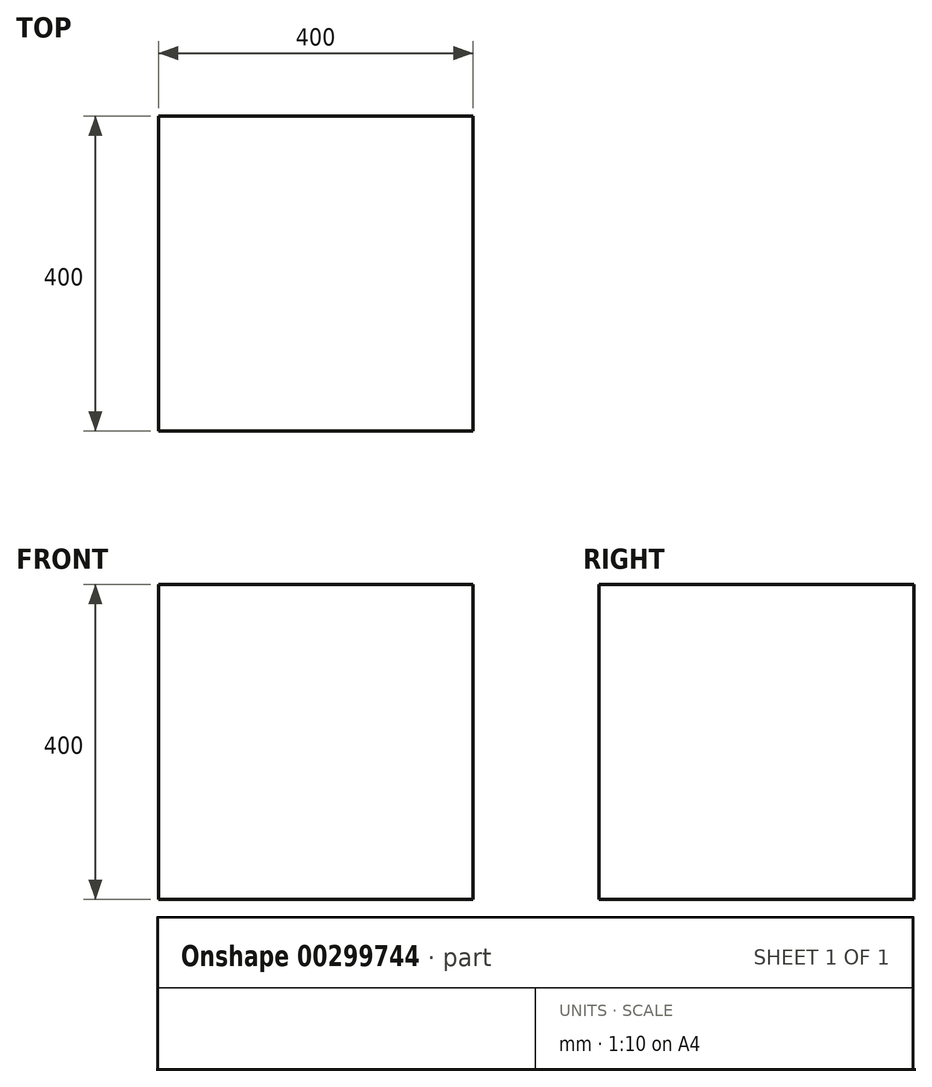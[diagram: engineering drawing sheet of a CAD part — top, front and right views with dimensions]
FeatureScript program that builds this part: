
annotation { "Feature Type Name" : "Feature", "Feature Type Description" : "" }
export const myFeature = defineFeature(function(context is Context, id is Id, definition is map)
    precondition{}
    {
        {
            assignVariable(context, id + "F0", {"name" : "hauteur", "anyValue" : 380});
        }
        {
            var Q0;
            Q0=qCreatedBy(makeId("Top.planeOp"),FACE);
            var sketch = newSketch(context, id + "F1", { "sketchPlane" : qUnion([Q0])});
            skLineSegment(sketch, "E0.bottom", {"start": v(-200, 200) * mm, "end": v(200, 200) * mm});
            skLineSegment(sketch, "E0.top", {"start": v(-200, -200) * mm, "end": v(200, -200) * mm});
            skLineSegment(sketch, "E0.left", {"start": v(-200, 200) * mm, "end": v(-200, -200) * mm});
            skLineSegment(sketch, "E0.right", {"start": v(200, 200) * mm, "end": v(200, -200) * mm});
            skPoint(sketch, "E0.middle", {"position": v(0, 0) * mm});
            skSolve(sketch);
        }
        {
            var Q0;
            Q0=makeQuery(id+"F1.imprint","IMPRINT",FACE,{"disambiguationData":[TD([[makeQuery(id+"F1.imprint","IMPRINT",EDGE,{"derivedFrom":sQuery(id+"F1.wireOp",EDGE,"E0.bottom")}),-1.0]])]});
            extrude(context, id + "F2", {"entities" : qUnion([Q0]), "depth" : (getVariable(context, 'hauteur') + 20) * mm, "symmetric" : true});
        }
        {
            var Q0;
            Q0=makeQuery(id+"F2.opExtrude","CAP_FACE",FACE,{"disambiguationData":[OSD([sQuery(id+"F1.wireOp",EDGE,"E0.bottom"),sQuery(id+"F1.wireOp",EDGE,"E0.top"),sQuery(id+"F1.wireOp",EDGE,"E0.left"),sQuery(id+"F1.wireOp",EDGE,"E0.right")])],"isStart":true});
            var sketch = newSketch(context, id + "F3", { "sketchPlane" : qUnion([Q0])});
            skLineSegment(sketch, "E1", {"start": v(-200, -190) * mm, "end": v(-200, 190) * mm, "construction": true});
            skLineSegment(sketch, "E2", {"start": v(-190, 200) * mm, "end": v(190, 200) * mm, "construction": true});
            skLineSegment(sketch, "E3", {"start": v(200, 190) * mm, "end": v(200, -190) * mm, "construction": true});
            skLineSegment(sketch, "E4", {"start": v(190, -200) * mm, "end": v(-190, -200) * mm, "construction": true});
            skCircle(sketch, "E5", {"center": v(-200, 200) * mm, "radius": 10 * mm, "construction": true});
            skCircle(sketch, "E6", {"center": v(-200, -200) * mm, "radius": 10 * mm, "construction": true});
            skSolve(sketch);
        }
        {
            var Q0;
            Q0=makeQuery(id+"F2.opExtrude","CAP_FACE",FACE,{"disambiguationData":[OSD([sQuery(id+"F1.wireOp",EDGE,"E0.bottom"),sQuery(id+"F1.wireOp",EDGE,"E0.top"),sQuery(id+"F1.wireOp",EDGE,"E0.left"),sQuery(id+"F1.wireOp",EDGE,"E0.right")])],"isStart":false});
            var sketch = newSketch(context, id + "F4", { "sketchPlane" : qUnion([Q0])});
            skLineSegment(sketch, "E7", {"start": v(-200, -190) * mm, "end": v(-200, 190) * mm, "construction": true});
            skLineSegment(sketch, "E8", {"start": v(-190, 200) * mm, "end": v(190, 200) * mm, "construction": true});
            skLineSegment(sketch, "E9", {"start": v(200, 190) * mm, "end": v(200, -190) * mm, "construction": true});
            skLineSegment(sketch, "E10", {"start": v(190, -200) * mm, "end": v(-190, -200) * mm, "construction": true});
            skSolve(sketch);
        }
        {
            var Q0;
            Q0=makeQuery(id+"F2.opExtrude","SWEPT_FACE",FACE,{"disambiguationData":[OSD([sQuery(id+"F1.wireOp",EDGE,"E0.left")])]});
            var sketch = newSketch(context, id + "F5", { "sketchPlane" : qUnion([Q0])});
            skCircle(sketch, "E11", {"center": v(200, -200) * mm, "radius": 10 * mm, "construction": true});
            skCircle(sketch, "E12", {"center": v(-200, 200) * mm, "radius": 10 * mm, "construction": true});
            skLineSegment(sketch, "E13", {"start": v(200, 190) * mm, "end": v(200, -190) * mm, "construction": true});
            skLineSegment(sketch, "E14", {"start": v(-200, 190) * mm, "end": v(-200, -190) * mm, "construction": true});
            skSolve(sketch);
        }
        {
            var Q0;
            Q0=qCreatedBy(makeId("Top.planeOp"),FACE);
            var sketch = newSketch(context, id + "F6", { "sketchPlane" : qUnion([Q0])});
            skLineSegment(sketch, "E15", {"start": v(0, 0) * mm, "end": v(-200, 0) * mm, "construction": true});
            skLineSegment(sketch, "E16", {"start": v(0, 200) * mm, "end": v(0, 0) * mm, "construction": true});
            skLineSegment(sketch, "E17", {"start": v(0, 0) * mm, "end": v(200, 0) * mm, "construction": true});
            skLineSegment(sketch, "E18", {"start": v(0, -200) * mm, "end": v(0, 0) * mm, "construction": true});
            skSolve(sketch);
        }
        {
            var Q0;
            Q0=qCreatedBy(makeId("Front.planeOp"),FACE);
            var sketch = newSketch(context, id + "F7", { "sketchPlane" : qUnion([Q0])});
            skLineSegment(sketch, "E19", {"start": v(0, 0) * mm, "end": v(0, 200) * mm, "construction": true});
            skLineSegment(sketch, "E20", {"start": v(0, 0) * mm, "end": v(0, -200) * mm, "construction": true});
            skSolve(sketch);
        }
        {
            var Q0;
            Q0=makeQuery(id+"F4.imprint","IMPRINT",FACE,{"disambiguationData":[TD([[makeQuery(id+"F4.imprint","IMPRINT",EDGE,{"derivedFrom":makeQuery(id+"F2.opExtrude","CAP_EDGE",EDGE,{"disambiguationData":[OSD([sQuery(id+"F1.wireOp",EDGE,"E0.bottom")])],"isStart":false})}),-1.0]])]});
            cPlane(context, id + "F8", {"entities" : qUnion([Q0]), "cplaneType" : CPlaneType.OFFSET, "offset" : 70 * mm, "oppositeDirection" : true, "width" : 150 * mm, "height" : 150 * mm});
        }
        {
            var Q0;
            Q0=qCreatedBy(id+"F8.planeOp",FACE);
            var sketch = newSketch(context, id + "F9", { "sketchPlane" : qUnion([Q0])});
            skLineSegment(sketch, "E21.bottom", {"start": v(-185, 204.5) * mm, "end": v(-151.7, 204.5) * mm});
            skLineSegment(sketch, "E21.top", {"start": v(-185, 162.2) * mm, "end": v(-151.7, 162.2) * mm});
            skLineSegment(sketch, "E21.left", {"start": v(-189.5, 200) * mm, "end": v(-189.5, 166.7) * mm});
            skLineSegment(sketch, "E21.right", {"start": v(-147.2, 200) * mm, "end": v(-147.2, 166.7) * mm});
            skCircle(sketch, "E22", {"center": v(-168.35, 183.35) * mm, "radius": 2.5 * mm});
            skCircle(sketch, "E23", {"center": v(-183.85, 198.85) * mm, "radius": 1.5 * mm});
            skCircle(sketch, "E24", {"center": v(-152.85, 198.85) * mm, "radius": 1.5 * mm});
            skCircle(sketch, "E25", {"center": v(-152.85, 167.85) * mm, "radius": 1.5 * mm});
            skCircle(sketch, "E26", {"center": v(-183.85, 167.85) * mm, "radius": 1.5 * mm});
            skArc(sketch, "E27", {"start": v(-189.5, 166.7) * mm, "mid": v(-187.38, 164.32) * mm, "end": v(-185, 162.2) * mm});
            skArc(sketch, "E28.trimOffspring", {"start": v(-185, 204.5) * mm, "mid": v(-187.38, 202.38) * mm, "end": v(-189.5, 200) * mm});
            skArc(sketch, "E29.trimOffspring", {"start": v(-147.2, 200) * mm, "mid": v(-149.32, 202.38) * mm, "end": v(-151.7, 204.5) * mm});
            skArc(sketch, "E30.trimOffspring", {"start": v(-151.7, 162.2) * mm, "mid": v(-149.32, 164.32) * mm, "end": v(-147.2, 166.7) * mm});
            skLineSegment(sketch, "E31", {"start": v(-170.35, 184.85) * mm, "end": v(-170.35, 181.85) * mm});
            skCircle(sketch, "E32", {"center": v(-168.35, 183.35) * mm, "radius": 11 * mm});
            skCircle(sketch, "E33", {"center": v(-168.35, 183.35) * mm, "radius": 16.15 * mm});
            skLineSegment(sketch, "E34", {"start": v(-168.35, 194.35) * mm, "end": v(-168.35, 172.35) * mm, "construction": true});
            skLineSegment(sketch, "E35", {"start": v(-179.35, 183.35) * mm, "end": v(-157.35, 183.35) * mm, "construction": true});
            skLineSegment(sketch, "E36.bottom", {"start": v(-183.85, 198.85) * mm, "end": v(-152.85, 198.85) * mm, "construction": true});
            skLineSegment(sketch, "E36.top", {"start": v(-183.85, 167.85) * mm, "end": v(-152.85, 167.85) * mm, "construction": true});
            skLineSegment(sketch, "E36.left", {"start": v(-183.85, 198.85) * mm, "end": v(-183.85, 167.85) * mm, "construction": true});
            skLineSegment(sketch, "E36.right", {"start": v(-152.85, 198.85) * mm, "end": v(-152.85, 167.85) * mm, "construction": true});
            skLineSegment(sketch, "E37.0.1.0", {"start": v(-147.2, 16.65) * mm, "end": v(-147.2, -16.65) * mm});
            skLineSegment(sketch, "E37.0.1.1", {"start": v(-185, -21.15) * mm, "end": v(-151.7, -21.15) * mm});
            skCircle(sketch, "E37.0.1.2", {"center": v(-168.35, 0) * mm, "radius": 11 * mm});
            skLineSegment(sketch, "E37.0.1.3", {"start": v(-185, 21.15) * mm, "end": v(-151.7, 21.15) * mm});
            skArc(sketch, "E37.0.1.4", {"start": v(-185, 21.15) * mm, "mid": v(-187.38, 19.03) * mm, "end": v(-189.5, 16.65) * mm});
            skCircle(sketch, "E37.0.1.5", {"center": v(-168.35, 0) * mm, "radius": 16.15 * mm});
            skLineSegment(sketch, "E37.0.1.6", {"start": v(-189.5, 16.65) * mm, "end": v(-189.5, -16.65) * mm});
            skPoint(sketch, "E37.0.1.7", {"position": v(-168.35, 0) * mm});
            skArc(sketch, "E37.0.1.8", {"start": v(-147.2, 16.65) * mm, "mid": v(-149.32, 19.03) * mm, "end": v(-151.7, 21.15) * mm});
            skCircle(sketch, "E37.0.1.9", {"center": v(-168.35, 0) * mm, "radius": 2.5 * mm});
            skArc(sketch, "E37.0.1.10", {"start": v(-189.5, -16.65) * mm, "mid": v(-187.38, -19.03) * mm, "end": v(-185, -21.15) * mm});
            skArc(sketch, "E37.0.1.11", {"start": v(-151.7, -21.15) * mm, "mid": v(-149.32, -19.03) * mm, "end": v(-147.2, -16.65) * mm});
            skCircle(sketch, "E37.0.1.12", {"center": v(-152.85, -15.5) * mm, "radius": 1.5 * mm});
            skCircle(sketch, "E37.0.1.13", {"center": v(-183.85, -15.5) * mm, "radius": 1.5 * mm});
            skCircle(sketch, "E37.0.1.14", {"center": v(-152.85, 15.5) * mm, "radius": 1.5 * mm});
            skCircle(sketch, "E37.0.1.15", {"center": v(-183.85, 15.5) * mm, "radius": 1.5 * mm});
            skLineSegment(sketch, "E37.0.1.16", {"start": v(-170.35, 1.5) * mm, "end": v(-170.35, -1.5) * mm});
            skLineSegment(sketch, "E37.0.2.0", {"start": v(-147.2, -166.7) * mm, "end": v(-147.2, -200) * mm});
            skLineSegment(sketch, "E37.0.2.1", {"start": v(-185, -204.5) * mm, "end": v(-151.7, -204.5) * mm});
            skCircle(sketch, "E37.0.2.2", {"center": v(-168.35, -183.35) * mm, "radius": 11 * mm});
            skLineSegment(sketch, "E37.0.2.3", {"start": v(-185, -162.2) * mm, "end": v(-151.7, -162.2) * mm});
            skArc(sketch, "E37.0.2.4", {"start": v(-185, -162.2) * mm, "mid": v(-187.38, -164.32) * mm, "end": v(-189.5, -166.7) * mm});
            skCircle(sketch, "E37.0.2.5", {"center": v(-168.35, -183.35) * mm, "radius": 16.15 * mm});
            skLineSegment(sketch, "E37.0.2.6", {"start": v(-189.5, -166.7) * mm, "end": v(-189.5, -200) * mm});
            skPoint(sketch, "E37.0.2.7", {"position": v(-168.35, -183.35) * mm});
            skArc(sketch, "E37.0.2.8", {"start": v(-147.2, -166.7) * mm, "mid": v(-149.32, -164.32) * mm, "end": v(-151.7, -162.2) * mm});
            skCircle(sketch, "E37.0.2.9", {"center": v(-168.35, -183.35) * mm, "radius": 2.5 * mm});
            skArc(sketch, "E37.0.2.10", {"start": v(-189.5, -200) * mm, "mid": v(-187.38, -202.38) * mm, "end": v(-185, -204.5) * mm});
            skArc(sketch, "E37.0.2.11", {"start": v(-151.7, -204.5) * mm, "mid": v(-149.32, -202.38) * mm, "end": v(-147.2, -200) * mm});
            skCircle(sketch, "E37.0.2.12", {"center": v(-152.85, -198.85) * mm, "radius": 1.5 * mm});
            skCircle(sketch, "E37.0.2.13", {"center": v(-183.85, -198.85) * mm, "radius": 1.5 * mm});
            skCircle(sketch, "E37.0.2.14", {"center": v(-152.85, -167.85) * mm, "radius": 1.5 * mm});
            skCircle(sketch, "E37.0.2.15", {"center": v(-183.85, -167.85) * mm, "radius": 1.5 * mm});
            skLineSegment(sketch, "E37.0.2.16", {"start": v(-170.35, -181.85) * mm, "end": v(-170.35, -184.85) * mm});
            skLineSegment(sketch, "E37.direction1", {"start": v(-200, 162.2) * mm, "end": v(-185, 162.2) * mm, "construction": true});
            skLineSegment(sketch, "E37.direction2", {"start": v(-185, 162.2) * mm, "end": v(-185, -21.15) * mm, "construction": true});
            skSolve(sketch);
        }
        {
            var Q0;
            Q0=qCreatedBy(id+"F8.planeOp",FACE);
            var sketch = newSketch(context, id + "F10", { "sketchPlane" : qUnion([Q0])});
            skLineSegment(sketch, "E38.bottom", {"start": v(41, 11.6) * mm, "end": v(41, 8.75) * mm});
            skLineSegment(sketch, "E38.top", {"start": v(26, 11.6) * mm, "end": v(26, 8.75) * mm});
            skLineSegment(sketch, "E38.left", {"start": v(40.6, 12) * mm, "end": v(26.4, 12) * mm});
            skLineSegment(sketch, "E38.right", {"start": v(40.6, -12) * mm, "end": v(26.4, -12) * mm});
            skLineSegment(sketch, "E39.bottom", {"start": v(37.5, 161) * mm, "end": v(37.5, 12) * mm});
            skLineSegment(sketch, "E39.top", {"start": v(29.5, 161) * mm, "end": v(29.5, 12) * mm});
            skLineSegment(sketch, "E39.left", {"start": v(37.5, 161) * mm, "end": v(29.5, 161) * mm});
            skLineSegment(sketch, "E39.right", {"start": v(37.5, -161) * mm, "end": v(29.5, -161) * mm});
            skLineSegment(sketch, "E40", {"start": v(40.6, 12) * mm, "end": v(41, 11.6) * mm});
            skLineSegment(sketch, "E41", {"start": v(26.4, 12) * mm, "end": v(26, 11.6) * mm});
            skLineSegment(sketch, "E42", {"start": v(26.4, -12) * mm, "end": v(26, -11.6) * mm});
            skLineSegment(sketch, "E43", {"start": v(40.6, -12) * mm, "end": v(41, -11.6) * mm});
            skLineSegment(sketch, "E44.bottom", {"start": v(39.9, 8.75) * mm, "end": v(39.9, 7.65) * mm});
            skLineSegment(sketch, "E45.bottom", {"start": v(27.1, 8.75) * mm, "end": v(27.1, 7.65) * mm});
            skLineSegment(sketch, "E46.bottom", {"start": v(27.1, -7.65) * mm, "end": v(27.1, -8.75) * mm});
            skLineSegment(sketch, "E47.bottom", {"start": v(39.9, -7.65) * mm, "end": v(39.9, -8.75) * mm});
            skLineSegment(sketch, "E48.trimOffspring", {"start": v(41, 7.65) * mm, "end": v(41, -7.65) * mm});
            skLineSegment(sketch, "E49.trimOffspring", {"start": v(41, -8.75) * mm, "end": v(41, -11.6) * mm});
            skLineSegment(sketch, "E50.trimOffspring", {"start": v(26, -8.75) * mm, "end": v(26, -11.6) * mm});
            skLineSegment(sketch, "E51.trimOffspring", {"start": v(26, 7.65) * mm, "end": v(26, -7.65) * mm});
            skLineSegment(sketch, "E52.trimOffspring", {"start": v(37.5, -12) * mm, "end": v(37.5, -161) * mm});
            skLineSegment(sketch, "E53.trimOffspring", {"start": v(29.5, -12) * mm, "end": v(29.5, -161) * mm});
            skLineSegment(sketch, "E54", {"start": v(37.5, 12) * mm, "end": v(37.5, -12) * mm, "construction": true});
            skLineSegment(sketch, "E55", {"start": v(29.5, -12) * mm, "end": v(29.5, 12) * mm, "construction": true});
            skLineSegment(sketch, "E56", {"start": v(41, 11.6) * mm, "end": v(26, 11.6) * mm});
            skLineSegment(sketch, "E57", {"start": v(41, -11.6) * mm, "end": v(26, -11.6) * mm});
            skLineSegment(sketch, "E58", {"start": v(26, 8.75) * mm, "end": v(41, 8.75) * mm});
            skLineSegment(sketch, "E59", {"start": v(41, 7.65) * mm, "end": v(26, 7.65) * mm});
            skLineSegment(sketch, "E60", {"start": v(26, -7.65) * mm, "end": v(41, -7.65) * mm});
            skLineSegment(sketch, "E61", {"start": v(41, -8.75) * mm, "end": v(26, -8.75) * mm});
            skLineSegment(sketch, "E62", {"start": v(0, 0) * mm, "end": v(33.5, 0) * mm, "construction": true});
            skLineSegment(sketch, "E63", {"start": v(0, 0) * mm, "end": v(-33.5, 0) * mm, "construction": true});
            skLineSegment(sketch, "E64.MirrorCS", {"start": v(-40.6, 12) * mm, "end": v(-41, 11.6) * mm});
            skLineSegment(sketch, "E65.MirrorCS", {"start": v(-39.9, 8.75) * mm, "end": v(-39.9, 7.65) * mm});
            skLineSegment(sketch, "E66.MirrorCS", {"start": v(-41, 11.6) * mm, "end": v(-41, 8.75) * mm});
            skLineSegment(sketch, "E67.MirrorCS", {"start": v(-26, 11.6) * mm, "end": v(-26, 8.75) * mm});
            skLineSegment(sketch, "E68.MirrorCS", {"start": v(-39.9, -7.65) * mm, "end": v(-39.9, -8.75) * mm});
            skLineSegment(sketch, "E69.MirrorCS", {"start": v(-26.4, 12) * mm, "end": v(-26, 11.6) * mm});
            skLineSegment(sketch, "E70.MirrorCS", {"start": v(-41, -8.75) * mm, "end": v(-41, -11.6) * mm});
            skLineSegment(sketch, "E71.MirrorCS", {"start": v(-27.1, 8.75) * mm, "end": v(-27.1, 7.65) * mm});
            skLineSegment(sketch, "E72.MirrorCS", {"start": v(-40.6, -12) * mm, "end": v(-41, -11.6) * mm});
            skLineSegment(sketch, "E73.MirrorCS", {"start": v(-26, -8.75) * mm, "end": v(-26, -11.6) * mm});
            skLineSegment(sketch, "E74.MirrorCS", {"start": v(-27.1, -7.65) * mm, "end": v(-27.1, -8.75) * mm});
            skLineSegment(sketch, "E75.MirrorCS", {"start": v(-26.4, -12) * mm, "end": v(-26, -11.6) * mm});
            skLineSegment(sketch, "E76.MirrorCS", {"start": v(-40.6, -12) * mm, "end": v(-26.4, -12) * mm});
            skLineSegment(sketch, "E77.MirrorCS", {"start": v(-41, -11.6) * mm, "end": v(-26, -11.6) * mm});
            skLineSegment(sketch, "E78.MirrorCS", {"start": v(-41, 11.6) * mm, "end": v(-26, 11.6) * mm});
            skLineSegment(sketch, "E79.MirrorCS", {"start": v(-40.6, 12) * mm, "end": v(-26.4, 12) * mm});
            skLineSegment(sketch, "E80.MirrorCS", {"start": v(-37.5, 161) * mm, "end": v(-29.5, 161) * mm});
            skLineSegment(sketch, "E81.MirrorCS", {"start": v(-37.5, -161) * mm, "end": v(-29.5, -161) * mm});
            skLineSegment(sketch, "E82.MirrorCS", {"start": v(-41, -8.75) * mm, "end": v(-26, -8.75) * mm});
            skLineSegment(sketch, "E83.MirrorCS", {"start": v(-26, 8.75) * mm, "end": v(-41, 8.75) * mm});
            skLineSegment(sketch, "E84.MirrorCS", {"start": v(-29.5, -12) * mm, "end": v(-29.5, 12) * mm, "construction": true});
            skLineSegment(sketch, "E85.MirrorCS", {"start": v(-37.5, 12) * mm, "end": v(-37.5, -12) * mm, "construction": true});
            skLineSegment(sketch, "E86.MirrorCS", {"start": v(-26, 7.65) * mm, "end": v(-26, -7.65) * mm});
            skLineSegment(sketch, "E87.MirrorCS", {"start": v(-29.5, 161) * mm, "end": v(-29.5, 12) * mm});
            skLineSegment(sketch, "E88.MirrorCS", {"start": v(-26, -7.65) * mm, "end": v(-41, -7.65) * mm});
            skLineSegment(sketch, "E89.MirrorCS", {"start": v(-41, 7.65) * mm, "end": v(-41, -7.65) * mm});
            skLineSegment(sketch, "E90.MirrorCS", {"start": v(-29.5, -12) * mm, "end": v(-29.5, -161) * mm});
            skLineSegment(sketch, "E91.MirrorCS", {"start": v(-41, 7.65) * mm, "end": v(-26, 7.65) * mm});
            skLineSegment(sketch, "E92.MirrorCS", {"start": v(-37.5, 161) * mm, "end": v(-37.5, 12) * mm});
            skLineSegment(sketch, "E93.MirrorCS", {"start": v(-37.5, -12) * mm, "end": v(-37.5, -161) * mm});
            skLineSegment(sketch, "E94.bottom", {"start": v(-25, 15) * mm, "end": v(25, 15) * mm, "construction": true});
            skLineSegment(sketch, "E94.top", {"start": v(-25, -15) * mm, "end": v(25, -15) * mm, "construction": true});
            skLineSegment(sketch, "E94.left", {"start": v(-25, 15) * mm, "end": v(-25, -15) * mm, "construction": true});
            skLineSegment(sketch, "E94.right", {"start": v(25, 15) * mm, "end": v(25, -15) * mm, "construction": true});
            skLineSegment(sketch, "E95", {"start": v(-26, 5) * mm, "end": v(-25, 5) * mm, "construction": true});
            skLineSegment(sketch, "E96", {"start": v(-26, -5) * mm, "end": v(-25, -5) * mm, "construction": true});
            skLineSegment(sketch, "E97", {"start": v(25, -5) * mm, "end": v(26, -5) * mm, "construction": true});
            skLineSegment(sketch, "E98", {"start": v(25, 5) * mm, "end": v(26, 5) * mm, "construction": true});
            skSolve(sketch);
        }
        {
            var Q0;
            Q0=qCreatedBy(id+"F8.planeOp",FACE);
            var sketch = newSketch(context, id + "F11", { "sketchPlane" : qUnion([Q0])});
            skLineSegment(sketch, "E99.bottom", {"start": v(-37.5, 161) * mm, "end": v(-29.5, 161) * mm, "construction": true});
            skLineSegment(sketch, "E99.left", {"start": v(-37.5, 161) * mm, "end": v(-37.5, 141.2) * mm, "construction": true});
            skLineSegment(sketch, "E99.right", {"start": v(-29.5, 161) * mm, "end": v(-29.5, 141.2) * mm, "construction": true});
            skLineSegment(sketch, "E100.bottom", {"start": v(29.5, 161) * mm, "end": v(37.5, 161) * mm, "construction": true});
            skLineSegment(sketch, "E100.left", {"start": v(29.5, 161) * mm, "end": v(29.5, 141.2) * mm, "construction": true});
            skLineSegment(sketch, "E100.right", {"start": v(37.5, 161) * mm, "end": v(37.5, 141.2) * mm, "construction": true});
            skLineSegment(sketch, "E101.0", {"start": v(-37.7, 161.2) * mm, "end": v(-37.7, 141.2) * mm});
            skLineSegment(sketch, "E101.1", {"start": v(-37.7, 161.2) * mm, "end": v(-29.3, 161.2) * mm});
            skLineSegment(sketch, "E101.2", {"start": v(-29.3, 161.2) * mm, "end": v(-29.3, 141.2) * mm});
            skLineSegment(sketch, "E102.0", {"start": v(29.3, 161.2) * mm, "end": v(29.3, 141.2) * mm});
            skLineSegment(sketch, "E102.1", {"start": v(29.3, 161.2) * mm, "end": v(37.7, 161.2) * mm});
            skLineSegment(sketch, "E102.2", {"start": v(37.7, 161.2) * mm, "end": v(37.7, 141.2) * mm});
            skSolve(sketch);
        }
    });
